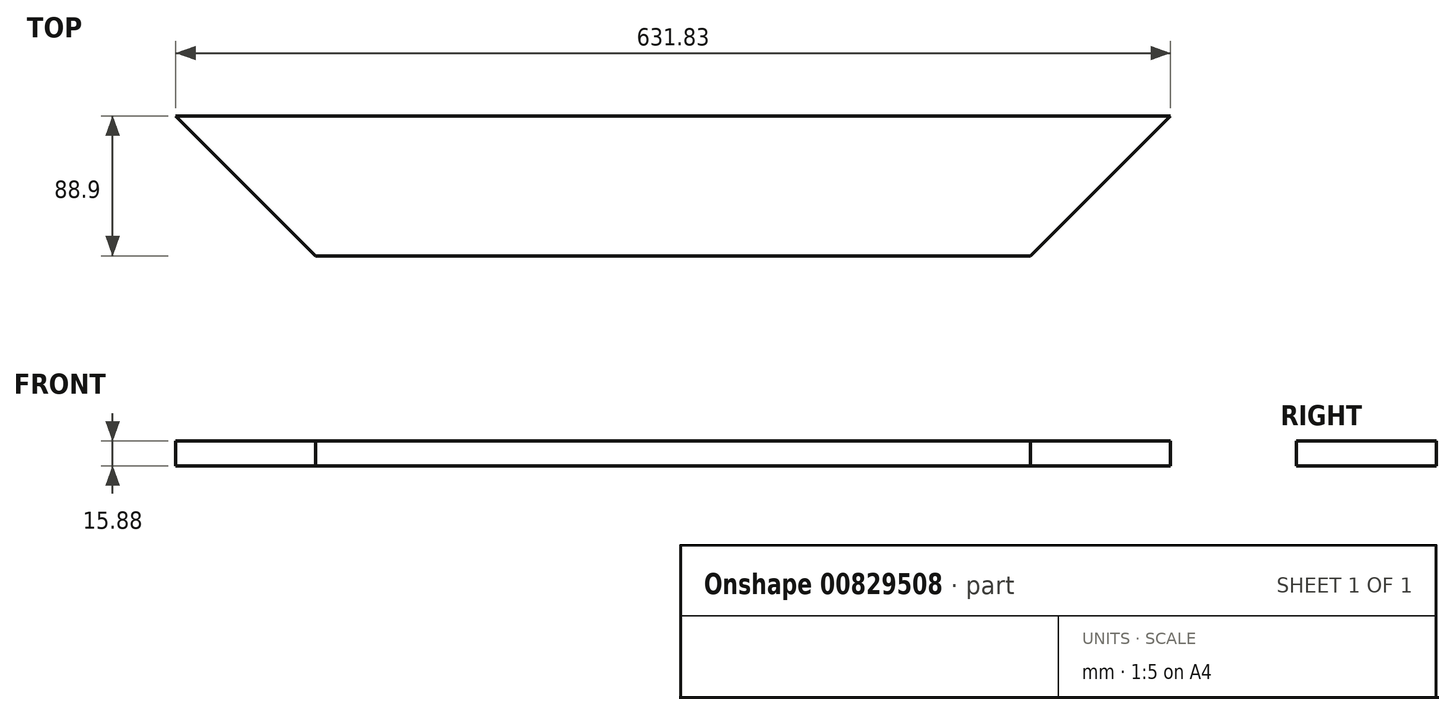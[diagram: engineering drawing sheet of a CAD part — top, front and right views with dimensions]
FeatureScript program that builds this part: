
annotation { "Feature Type Name" : "Feature", "Feature Type Description" : "" }
export const myFeature = defineFeature(function(context is Context, id is Id, definition is map)
    precondition{}
    {
        {
            var Q0;
            Q0=qCreatedBy(makeId("Top.planeOp"),FACE);
            var sketch = newSketch(context, id + "F0", { "sketchPlane" : qUnion([Q0])});
            skLineSegment(sketch, "E0.bottom", {"start": v(0, 0) * mm, "end": v(631.83, 0) * mm});
            skLineSegment(sketch, "E0.top", {"start": v(88.9, -88.9) * mm, "end": v(542.93, -88.9) * mm});
            skLineSegment(sketch, "E1", {"start": v(0, 0) * mm, "end": v(88.9, -88.9) * mm});
            skLineSegment(sketch, "E2", {"start": v(631.83, 0) * mm, "end": v(542.93, -88.9) * mm});
            skSolve(sketch);
        }
        {
            var Q0;
            Q0=makeQuery(id+"F0.imprint","IMPRINT",FACE,{"disambiguationData":[TD([[makeQuery(id+"F0.imprint","IMPRINT",EDGE,{"derivedFrom":sQuery(id+"F0.wireOp",EDGE,"E0.bottom")}),-1.0]])]});
            extrude(context, id + "F1", {"entities" : qUnion([Q0]), "depth" : 15.88 * mm, "offsetDistance" : 25.4 * mm});
        }
    });
